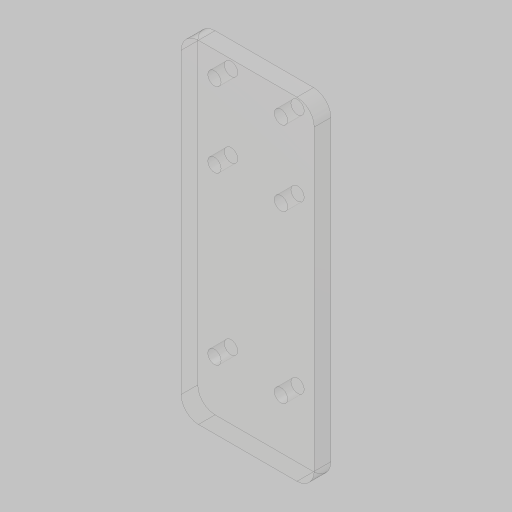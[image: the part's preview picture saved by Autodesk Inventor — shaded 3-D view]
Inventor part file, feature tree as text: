
AUTODESK INVENTOR PART (.ipt)
format: ipt  version: 2023.5 (Build 275446000, 446)  size: 110,080 bytes
history: native  units: in
note: dims shown in document units (in); Inventor stores cm internally (conversion verified against a paired STEP export)
features: sketch x1, extrude x1, hole x1, fillet x1
ambient origin geometry x8: Origin, YZ Plane, XZ Plane, XY Plane, X Axis, Y Axis, Z Axis, Center Point
bodies: Solid1 (feature_tree)
feature tree (4):
  sketch  "Sketch1"  dims[d0=2.0in d1=5.0in d2=0.375in d3=1.0in d4=1.5in d5=2.5in d6=0.25in d7=0.0in d8=0.201in d9=0.432in d10=0.385in d11=0.25in d12=0.5635in d13=1.0in d14=0.8108in d15=0.26in]
  extrude  "Extrusion1"  Depth=5.0in
  hole  "Hole1"  [1 undecoded]
  fillet  "Fillet1"  Radius=1.0in
note: 1 required parameter value undecoded (feature->parameter linkage not recoverable at this tier; creation-order binding heuristic only, values carry confidence <= 0.55)
